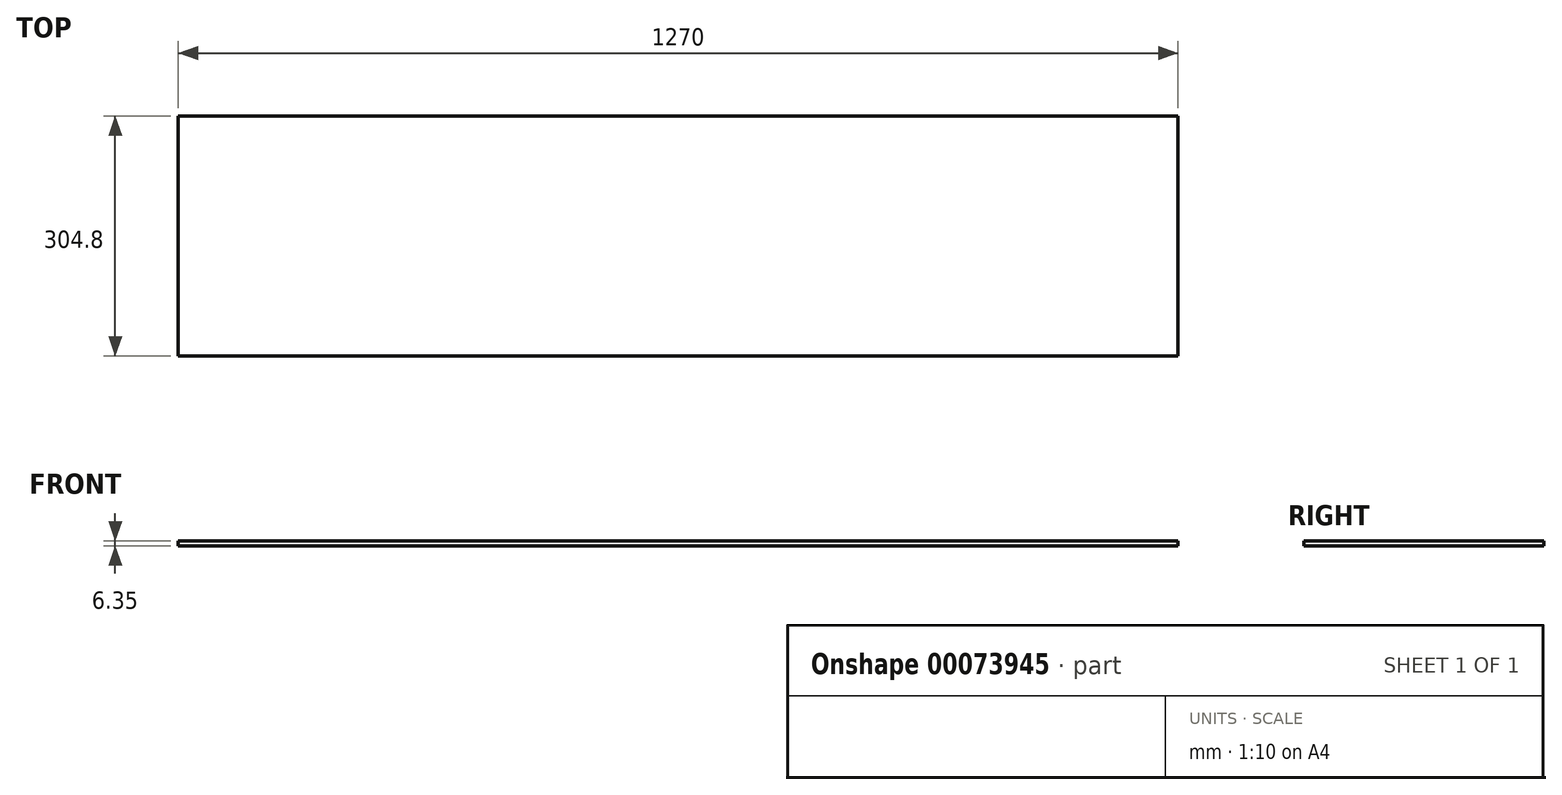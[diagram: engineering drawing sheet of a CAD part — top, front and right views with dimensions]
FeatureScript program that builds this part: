
annotation { "Feature Type Name" : "Feature", "Feature Type Description" : "" }
export const myFeature = defineFeature(function(context is Context, id is Id, definition is map)
    precondition{}
    {
        {
            var Q0;
            Q0=qCreatedBy(makeId("Top.planeOp"),FACE);
            var sketch = newSketch(context, id + "F0", { "sketchPlane" : qUnion([Q0])});
            skLineSegment(sketch, "E0.rect.bottom", {"start": v(-635, 152.4) * mm, "end": v(635, 152.4) * mm});
            skLineSegment(sketch, "E0.rect.top", {"start": v(-635, -152.4) * mm, "end": v(635, -152.4) * mm});
            skLineSegment(sketch, "E0.rect.left", {"start": v(-635, 152.4) * mm, "end": v(-635, -152.4) * mm});
            skLineSegment(sketch, "E0.rect.right", {"start": v(635, 152.4) * mm, "end": v(635, -152.4) * mm});
            skPoint(sketch, "E0.rect.middle", {"position": v(0, 0) * mm});
            skSolve(sketch);
        }
        {
            var Q0;
            Q0=makeQuery(id+"F0.imprint","IMPRINT",FACE,{"disambiguationData":[TD([[makeQuery(id+"F0.imprint","IMPRINT",EDGE,{"derivedFrom":sQuery(id+"F0.wireOp",EDGE,"E0.rect.bottom")}),-1.0]])]});
            extrude(context, id + "F1", {"entities" : qUnion([Q0]), "depth" : 6.35 * mm});
        }
    });
